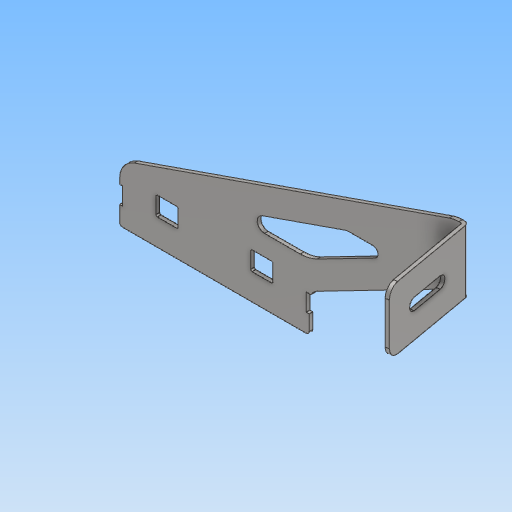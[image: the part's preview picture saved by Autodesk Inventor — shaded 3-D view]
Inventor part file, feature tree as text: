
AUTODESK INVENTOR PART (.ipt)
format: ipt  version: 2020 (Build 240168000, 168)  size: 209,920 bytes
history: native  units: mm
features: other x4, sketch x1, plane x1
ambient origin geometry x8: Origin, YZ Plane, XZ Plane, XY Plane, X Axis, Y Axis, Z Axis, Center Point
bodies: Body1 (feature_tree)
feature tree (6):
  other  "白鐵-吊架-短(R).ipt"
  other  "實體1::白鐵-吊架-短(R).ipt"
  other  "標籤特徵1"
  sketch  "草圖1"
  plane  "工作平面1"
  other  "實體1"
